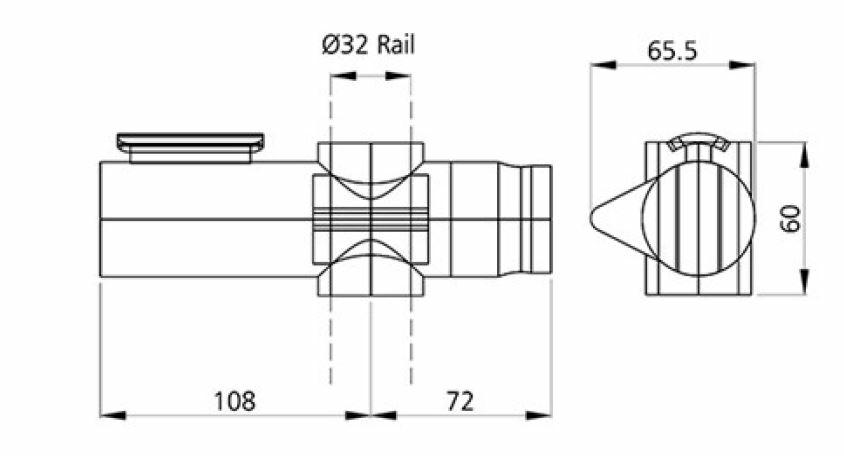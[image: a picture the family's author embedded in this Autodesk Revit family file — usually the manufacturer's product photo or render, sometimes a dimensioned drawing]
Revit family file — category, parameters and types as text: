
# Revit family: RBA4806-731
name_source: partatom
category: Plumbing Fixtures
units: mm (PartAtom-declared; Revit-internal decimal feet)

## family parameters
Always vertical = Yes
Cut with Voids When Loaded = No
Part Type = Normal
Room Calculation Point = No
Round Connector Dimension = Use Diameter
Shared = Yes
Work Plane-Based = No

## types (1)
- RBA4806-731
    CW Connection = Yes
    Default Elevation = 0 mm  [stored 0 ft]
    Description = Modular Shower Rail Kit, Brushed Brass
    Distance Away from Toilet (default) = 1090 mm  [stored 3.57612 ft]
    Distance Away from Wall (default) = 100 mm  [stored 0.328084 ft]
    HW Connection = Yes
    Manufacturer = RBA Group
    Materials & Finishes = PVD Gunmetal Stainless Steel
    Model = RBA4805-731
    OFFSET = 1000 mm  [stored 3.28084 ft]
    URL = www.rba.com.au
    Vent Connection = Yes
    Waste Connection = Yes

note: [stored X ft] marks values corroborated as IEEE doubles in the binary element streams (Revit-internal decimal feet)

## geometry (parser evidence)
native form markers: Blend x2, Sweep x5
no freeform markers — native parametric forms only
